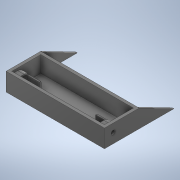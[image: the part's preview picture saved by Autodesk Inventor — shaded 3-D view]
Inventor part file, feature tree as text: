
AUTODESK INVENTOR PART (.ipt)
format: ipt  version: 2020 (Build 240168000, 168)  size: 273,920 bytes
history: native  units: in
note: dims shown in document units (in); Inventor stores cm internally (conversion verified against a paired STEP export)
features: extrude x6, sketch x6, projected_geometry x3, mirror x2
ambient origin geometry x8: Origin, YZ Plane, XZ Plane, XY Plane, X Axis, Y Axis, Z Axis, Center Point
bodies: Solid1 (feature_tree)
feature tree (17):
  extrude  "Extrusion1"  Depth=2.3622in
  extrude  "Extrusion2"  Depth=1.1024in TaperAngle=0.0deg
  extrude  "Extrusion5"  Depth=0.0787in
  extrude  "Extrusion6"  Depth=0.7874in TaperAngle=0.0deg
  extrude  "Extrusion7"  Depth=0.6693in
  mirror  "Mirror2"
  sketch  "Sketch14"  dims[d27=0.2756in d28=0.6693in]
  extrude  "Extrusion12"  Depth=0.1181in
  mirror  "Mirror5"
  sketch  "Sketch2"  dims[d0=6.6929in d1=2.3622in]
  projected_geometry  "Projected Loop1"
  sketch  "Sketch7"  dims[d2=0.1181in d3=0.0in d5=1.1024in d6=0.0in]
  sketch  "Sketch8"  dims[d18=0.6693in d20=0.0787in]
  projected_geometry  "Projected Loop5"
  sketch  "Sketch9"  dims[d21=0.4429in d22=0.0in d25=0.7874in d26=0.0in]
  sketch  "Sketch15"  dims[d30=0.4626in d31=0.0in d32=0.5906in d36=6.2992in d37=1.9685in d40=0.7874in d41=0.5906in d55=0.6102in d62=0.3937in d63=0.4724in d64=0.2362in d67=2.3622in d68=0.1181in d69=0.0in d50=0.0197in d51=0.0344in d52=0.0197in d53=0.0344in]
  projected_geometry  "Projected Loop6"
